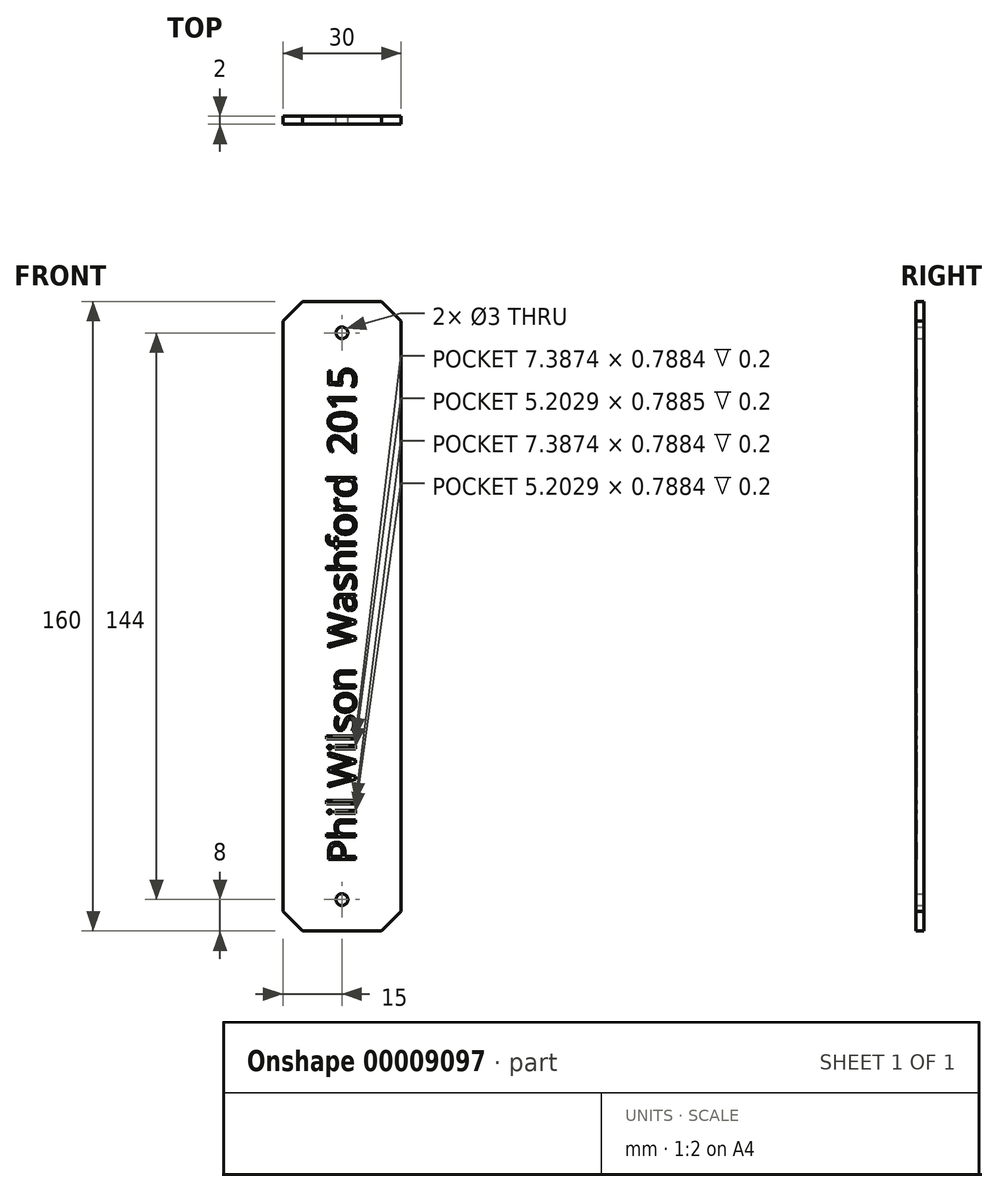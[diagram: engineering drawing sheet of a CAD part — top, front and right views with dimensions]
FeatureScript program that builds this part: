
annotation { "Feature Type Name" : "Feature", "Feature Type Description" : "" }
export const myFeature = defineFeature(function(context is Context, id is Id, definition is map)
    precondition{}
    {
        {
            var Q0;
            Q0=qCreatedBy(makeId("Front.planeOp"),FACE);
            var sketch = newSketch(context, id + "F0", { "sketchPlane" : qUnion([Q0])});
            skLineSegment(sketch, "E0.rect.bottom", {"start": v(80, -15) * mm, "end": v(-80, -15) * mm});
            skLineSegment(sketch, "E0.rect.top", {"start": v(80, 15) * mm, "end": v(-80, 15) * mm});
            skLineSegment(sketch, "E0.rect.left", {"start": v(80, -15) * mm, "end": v(80, 15) * mm});
            skLineSegment(sketch, "E0.rect.right", {"start": v(-80, -15) * mm, "end": v(-80, 15) * mm});
            skPoint(sketch, "E0.rect.middle", {"position": v(0, 0) * mm});
            skCircle(sketch, "E1", {"center": v(72, 0) * mm, "radius": 1.5 * mm});
            skPoint(sketch, "E1.centerSnap0", {"position": v(80, 0) * mm});
            skCircle(sketch, "E2", {"center": v(-72, 0) * mm, "radius": 1.5 * mm});
            skPoint(sketch, "E2.centerSnap0", {"position": v(-80, 0) * mm});
            skSolve(sketch);
        }
        {
            var Q0;
            Q0 = qSketchRegion(id + "F0", true);
            extrude(context, id + "F1", {"entities" : qUnion([Q0]), "depth" : 2 * mm});
        }
        {
            var Q0;
            Q0=makeQuery(id+"F1.opExtrude","CAP_FACE",FACE,{"disambiguationData":[OSD([sQuery(id+"F0.wireOp",EDGE,"E0.rect.bottom"),sQuery(id+"F0.wireOp",EDGE,"E0.rect.top"),sQuery(id+"F0.wireOp",EDGE,"E0.rect.left"),sQuery(id+"F0.wireOp",EDGE,"E0.rect.right")])],"isStart":false});
            var sketch = newSketch(context, id + "F2", { "sketchPlane" : qUnion([Q0])});
            skText(sketch, "E3", { "text": "Phil Wilson  Washford  2015", "fontName": "OpenSans-Regular.ttf"});
            skPoint(sketch, "E4", {"position": v(62.77, 0) * mm});
            const initialGuessF2  = {"E3": [-0.06277, -0.0035, 1, 0, 0.007]};
            skSetInitialGuess(sketch, initialGuessF2);
            skSolve(sketch);
        }
        {
            var Q0;
            Q0 = qSketchRegion(id + "F2", true);
            extrude(context, id + "F3", {"entities" : qUnion([Q0]), "operationType" : NewBodyOperationType.REMOVE, "oppositeDirection" : true, "depth" : 0.2 * mm});
        }
        {
            var Q0;
            Q0=makeQuery(id+"F1.opExtrude","SWEPT_BODY",BODY,{"disambiguationData":[OSD([sQuery(id+"F0.wireOp",EDGE,"E0.rect.bottom"),sQuery(id+"F0.wireOp",EDGE,"E0.rect.top"),sQuery(id+"F0.wireOp",EDGE,"E0.rect.left"),sQuery(id+"F0.wireOp",EDGE,"E0.rect.right")])]});
            var Q1;
            Q1=makeQuery(id+"F1.opExtrude","SWEPT_EDGE",EDGE,{"disambiguationData":[OSD([sQuery(id+"F0.wireOp",EDGE,"E0.rect.bottom"),sQuery(id+"F0.wireOp",EDGE,"E0.rect.right")])]});
            transform(context, id + "F4", {"entities" : qUnion([Q0]), "transformType" : TransformType.ROTATION, "transformAxis" : qUnion([Q1]), "angle" : 90 * degree, "oppositeDirection" : true, "makeCopy" : false});
        }
        {
            var Q0;
            Q0=makeQuery(id+"F1.opExtrude","SWEPT_EDGE",EDGE,{"disambiguationData":[OSD([sQuery(id+"F0.wireOp",EDGE,"E0.rect.top"),sQuery(id+"F0.wireOp",EDGE,"E0.rect.left")])]});
            var Q1;
            Q1=makeQuery(id+"F1.opExtrude","SWEPT_EDGE",EDGE,{"disambiguationData":[OSD([sQuery(id+"F0.wireOp",EDGE,"E0.rect.bottom"),sQuery(id+"F0.wireOp",EDGE,"E0.rect.left")])]});
            var Q2;
            Q2=makeQuery(id+"F1.opExtrude","SWEPT_EDGE",EDGE,{"disambiguationData":[OSD([sQuery(id+"F0.wireOp",EDGE,"E0.rect.top"),sQuery(id+"F0.wireOp",EDGE,"E0.rect.right")])]});
            var Q3;
            Q3=makeQuery(id+"F1.opExtrude","SWEPT_EDGE",EDGE,{"disambiguationData":[OSD([sQuery(id+"F0.wireOp",EDGE,"E0.rect.bottom"),sQuery(id+"F0.wireOp",EDGE,"E0.rect.right")])]});
            chamfer(context, id + "F5", {"entities" : qUnion([Q0, Q1, Q2, Q3]), "width" : 5 * mm, "tangentPropagation" : true});
        }
    });
